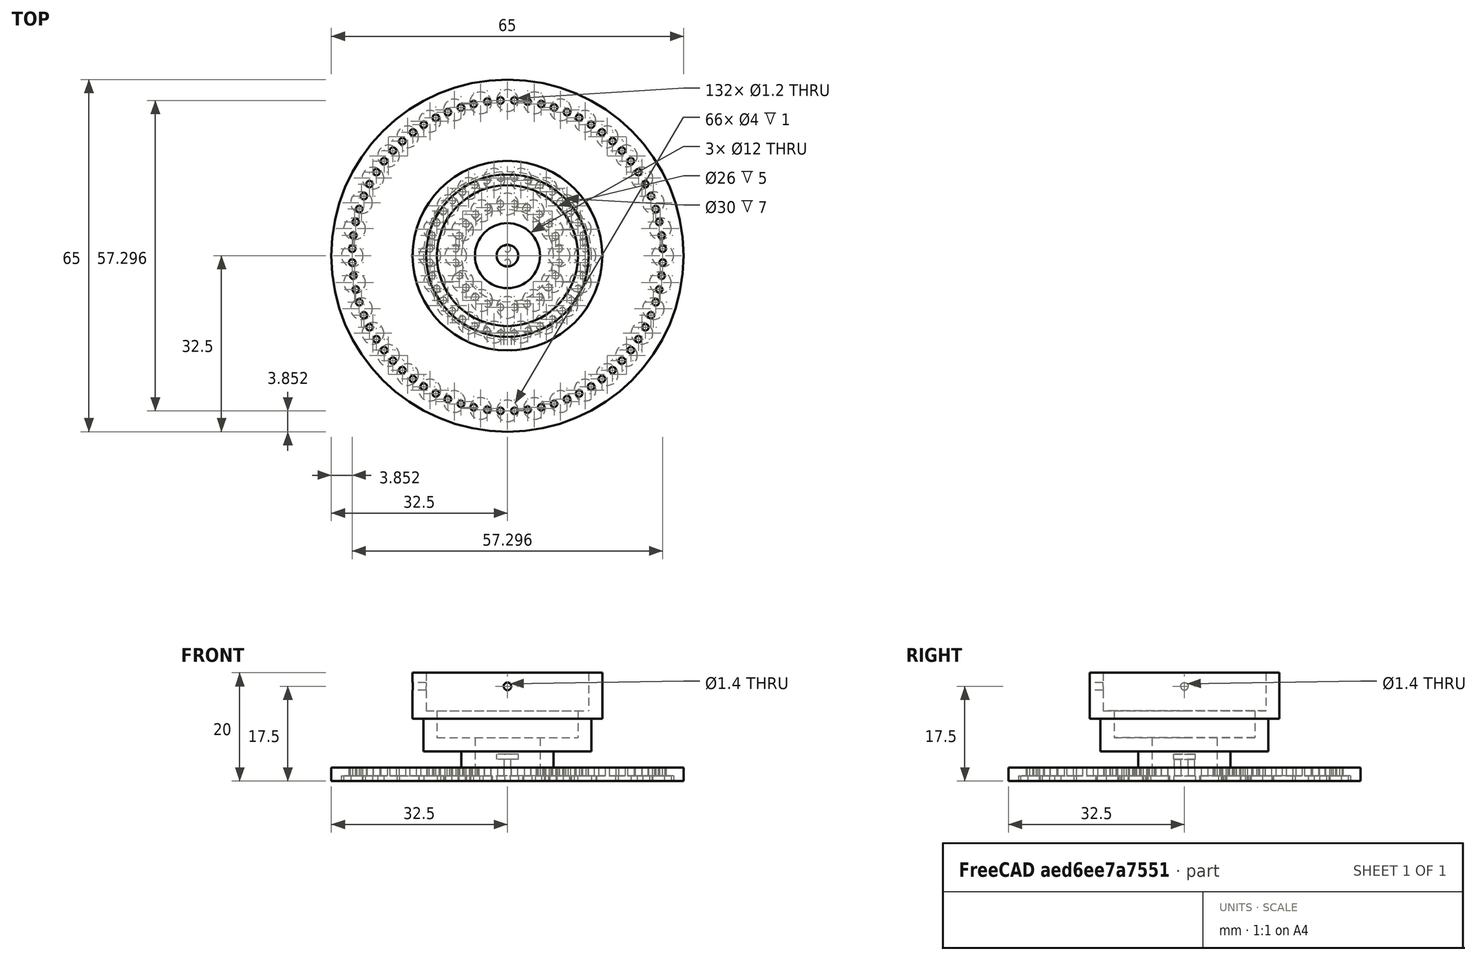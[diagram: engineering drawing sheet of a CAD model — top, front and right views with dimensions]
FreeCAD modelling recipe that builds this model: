
FCSTD DOCUMENT  (FreeCAD 0.16R6706 (Git))
Label: S2H-LED-ring-illuminator
License: All rights reserved
LicenseURL: http://en.wikipedia.org/wiki/All_rights_reserved
objects: Part::Cylinder×209, Part::MultiFuse×71, Part::Cut×7, Part::Thickness×3
note: 290 computed .brp shape members not serialized (recipe doc carries the construction recipe); baked Part::Feature solids carry a one-line shape summary decoded from their .brp

FEATURE [Part::Cylinder] Cylinder  label="grid base"
  Angle = 360
  Height = 2.5
  Radius = 32.5
FEATURE [Part::Cylinder] Cylinder001  label="cam slot"
  Angle = 360
  Height = 2.5
  Radius = 6
FEATURE [Part::Cut] Cut  label="grid plate"
  Base = -> Cylinder
  Tool = -> Cylinder001
FEATURE [Part::Cylinder] Cylinder002
  Angle = 360
  Height = 1
  Placement = pos=(0,0,1.5) rot=(0,0,1;0rad)
  Radius = 2
FEATURE [Part::Cylinder] Cylinder003
  Angle = 360
  Height = 2.5
  Placement = pos=(0,1.27,0) rot=(0,0,1;0rad)
  Radius = 0.6
FEATURE [Part::Cylinder] Cylinder004
  Angle = 360
  Height = 2.5
  Placement = pos=(0,-1.27,0) rot=(0,0,1;0rad)
  Radius = 0.6
FEATURE [Part::MultiFuse] Fusion  label="led slot template"
  Shapes = -> [Cylinder002,Cylinder003,Cylinder004]
FEATURE [Part::Cylinder] Cylinder005
  Angle = 360
  Height = 1
  Placement = pos=(0,0,1.5) rot=(0,0,1;0rad)
  Radius = 2
FEATURE [Part::Cylinder] Cylinder006
  Angle = 360
  Height = 2.5
  Placement = pos=(0,1.27,0) rot=(0,0,1;0rad)
  Radius = 0.6
FEATURE [Part::Cylinder] Cylinder007
  Angle = 360
  Height = 2.5
  Placement = pos=(0,-1.27,0) rot=(0,0,1;0rad)
  Radius = 0.6
FEATURE [Part::MultiFuse] Fusion001  label="led 1-01"
  Placement = pos=(9.5493,0,0) rot=(0,0,1;0rad)
  Shapes = -> [Cylinder005,Cylinder006,Cylinder007]
FEATURE [Part::Cylinder] Cylinder008
  Angle = 360
  Height = 1
  Placement = pos=(0,0,1.5) rot=(0,0,1;0rad)
  Radius = 2
FEATURE [Part::Cylinder] Cylinder009
  Angle = 360
  Height = 2.5
  Placement = pos=(0,1.27,0) rot=(0,0,1;0rad)
  Radius = 0.6
FEATURE [Part::Cylinder] Cylinder010
  Angle = 360
  Height = 2.5
  Placement = pos=(0,-1.27,0) rot=(0,0,1;0rad)
  Radius = 0.6
FEATURE [Part::MultiFuse] Fusion002  label="led 1-02"
  Placement = pos=(8.26993,4.77465,0) rot=(0,0,1;0.523599rad)
  Shapes = -> [Cylinder008,Cylinder009,Cylinder010]
FEATURE [Part::Cylinder] Cylinder011
  Angle = 360
  Height = 1
  Placement = pos=(0,0,1.5) rot=(0,0,1;0rad)
  Radius = 2
FEATURE [Part::Cylinder] Cylinder012
  Angle = 360
  Height = 2.5
  Placement = pos=(0,1.27,0) rot=(0,0,1;0rad)
  Radius = 0.6
FEATURE [Part::Cylinder] Cylinder013
  Angle = 360
  Height = 2.5
  Placement = pos=(0,-1.27,0) rot=(0,0,1;0rad)
  Radius = 0.6
FEATURE [Part::MultiFuse] Fusion003  label="led 1-03"
  Placement = pos=(4.77465,8.26993,0) rot=(0,0,1;1.0472rad)
  Shapes = -> [Cylinder011,Cylinder012,Cylinder013]
FEATURE [Part::Cylinder] Cylinder014
  Angle = 360
  Height = 1
  Placement = pos=(0,0,1.5) rot=(0,0,1;0rad)
  Radius = 2
FEATURE [Part::Cylinder] Cylinder015
  Angle = 360
  Height = 2.5
  Placement = pos=(0,1.27,0) rot=(0,0,1;0rad)
  Radius = 0.6
FEATURE [Part::Cylinder] Cylinder016
  Angle = 360
  Height = 2.5
  Placement = pos=(0,-1.27,0) rot=(0,0,1;0rad)
  Radius = 0.6
FEATURE [Part::MultiFuse] Fusion004  label="led 1-04"
  Placement = pos=(0,9.5493,0) rot=(0,0,1;1.5708rad)
  Shapes = -> [Cylinder014,Cylinder015,Cylinder016]
FEATURE [Part::Cylinder] Cylinder017
  Angle = 360
  Height = 1
  Placement = pos=(0,0,1.5) rot=(0,0,1;0rad)
  Radius = 2
FEATURE [Part::Cylinder] Cylinder018
  Angle = 360
  Height = 2.5
  Placement = pos=(0,1.27,0) rot=(0,0,1;0rad)
  Radius = 0.6
FEATURE [Part::Cylinder] Cylinder019
  Angle = 360
  Height = 2.5
  Placement = pos=(0,-1.27,0) rot=(0,0,1;0rad)
  Radius = 0.6
FEATURE [Part::MultiFuse] Fusion005  label="led 1-05"
  Placement = pos=(-4.77465,8.26993,0) rot=(0,0,1;2.0944rad)
  Shapes = -> [Cylinder017,Cylinder018,Cylinder019]
FEATURE [Part::Cylinder] Cylinder020
  Angle = 360
  Height = 1
  Placement = pos=(0,0,1.5) rot=(0,0,1;0rad)
  Radius = 2
FEATURE [Part::Cylinder] Cylinder021
  Angle = 360
  Height = 2.5
  Placement = pos=(0,1.27,0) rot=(0,0,1;0rad)
  Radius = 0.6
FEATURE [Part::Cylinder] Cylinder022
  Angle = 360
  Height = 2.5
  Placement = pos=(0,-1.27,0) rot=(0,0,1;0rad)
  Radius = 0.6
FEATURE [Part::MultiFuse] Fusion006  label="led 1-06"
  Placement = pos=(-8.26993,4.77465,0) rot=(0,0,1;2.61799rad)
  Shapes = -> [Cylinder020,Cylinder021,Cylinder022]
FEATURE [Part::Cylinder] Cylinder023
  Angle = 360
  Height = 1
  Placement = pos=(0,0,1.5) rot=(0,0,1;0rad)
  Radius = 2
FEATURE [Part::Cylinder] Cylinder024
  Angle = 360
  Height = 2.5
  Placement = pos=(0,1.27,0) rot=(0,0,1;0rad)
  Radius = 0.6
FEATURE [Part::Cylinder] Cylinder025
  Angle = 360
  Height = 2.5
  Placement = pos=(0,-1.27,0) rot=(0,0,1;0rad)
  Radius = 0.6
FEATURE [Part::MultiFuse] Fusion007  label="led 1-07"
  Placement = pos=(-9.5493,0,0) rot=(0,0,1;3.14159rad)
  Shapes = -> [Cylinder023,Cylinder024,Cylinder025]
FEATURE [Part::Cylinder] Cylinder026
  Angle = 360
  Height = 1
  Placement = pos=(0,0,1.5) rot=(0,0,1;0rad)
  Radius = 2
FEATURE [Part::Cylinder] Cylinder027
  Angle = 360
  Height = 2.5
  Placement = pos=(0,1.27,0) rot=(0,0,1;0rad)
  Radius = 0.6
FEATURE [Part::Cylinder] Cylinder028
  Angle = 360
  Height = 2.5
  Placement = pos=(0,-1.27,0) rot=(0,0,1;0rad)
  Radius = 0.6
FEATURE [Part::MultiFuse] Fusion008  label="led 1-08"
  Placement = pos=(-8.26993,-4.77465,0) rot=(0,0,1;3.66519rad)
  Shapes = -> [Cylinder026,Cylinder027,Cylinder028]
FEATURE [Part::Cylinder] Cylinder029
  Angle = 360
  Height = 1
  Placement = pos=(0,0,1.5) rot=(0,0,1;0rad)
  Radius = 2
FEATURE [Part::Cylinder] Cylinder030
  Angle = 360
  Height = 2.5
  Placement = pos=(0,1.27,0) rot=(0,0,1;0rad)
  Radius = 0.6
FEATURE [Part::Cylinder] Cylinder031
  Angle = 360
  Height = 2.5
  Placement = pos=(0,-1.27,0) rot=(0,0,1;0rad)
  Radius = 0.6
FEATURE [Part::MultiFuse] Fusion009  label="led 1-09"
  Placement = pos=(-4.77465,-8.26993,0) rot=(0,0,1;4.18879rad)
  Shapes = -> [Cylinder029,Cylinder030,Cylinder031]
FEATURE [Part::Cylinder] Cylinder032
  Angle = 360
  Height = 1
  Placement = pos=(0,0,1.5) rot=(0,0,1;0rad)
  Radius = 2
FEATURE [Part::Cylinder] Cylinder033
  Angle = 360
  Height = 2.5
  Placement = pos=(0,1.27,0) rot=(0,0,1;0rad)
  Radius = 0.6
FEATURE [Part::Cylinder] Cylinder034
  Angle = 360
  Height = 2.5
  Placement = pos=(0,-1.27,0) rot=(0,0,1;0rad)
  Radius = 0.6
FEATURE [Part::MultiFuse] Fusion010  label="led 1-10"
  Placement = pos=(0,-9.5493,0) rot=(0,0,-1;1.5708rad)
  Shapes = -> [Cylinder032,Cylinder033,Cylinder034]
FEATURE [Part::Cylinder] Cylinder035
  Angle = 360
  Height = 1
  Placement = pos=(0,0,1.5) rot=(0,0,1;0rad)
  Radius = 2
FEATURE [Part::Cylinder] Cylinder036
  Angle = 360
  Height = 2.5
  Placement = pos=(0,1.27,0) rot=(0,0,1;0rad)
  Radius = 0.6
FEATURE [Part::Cylinder] Cylinder037
  Angle = 360
  Height = 2.5
  Placement = pos=(0,-1.27,0) rot=(0,0,1;0rad)
  Radius = 0.6
FEATURE [Part::MultiFuse] Fusion011  label="led 1-11"
  Placement = pos=(4.77465,-8.26993,0) rot=(0,0,-1;1.0472rad)
  Shapes = -> [Cylinder035,Cylinder036,Cylinder037]
FEATURE [Part::Cylinder] Cylinder038
  Angle = 360
  Height = 1
  Placement = pos=(0,0,1.5) rot=(0,0,1;0rad)
  Radius = 2
FEATURE [Part::Cylinder] Cylinder039
  Angle = 360
  Height = 2.5
  Placement = pos=(0,1.27,0) rot=(0,0,1;0rad)
  Radius = 0.6
FEATURE [Part::Cylinder] Cylinder040
  Angle = 360
  Height = 2.5
  Placement = pos=(0,-1.27,0) rot=(0,0,1;0rad)
  Radius = 0.6
FEATURE [Part::MultiFuse] Fusion012  label="led 1-12"
  Placement = pos=(8.26993,-4.77465,0) rot=(0,0,-1;0.523599rad)
  Shapes = -> [Cylinder038,Cylinder039,Cylinder040]
FEATURE [Part::Cylinder] Cylinder041
  Angle = 360
  Height = 1
  Placement = pos=(0,0,1.5) rot=(0,0,1;0rad)
  Radius = 2
FEATURE [Part::Cylinder] Cylinder042
  Angle = 360
  Height = 2.5
  Placement = pos=(0,1.27,0) rot=(0,0,1;0rad)
  Radius = 0.6
FEATURE [Part::Cylinder] Cylinder043
  Angle = 360
  Height = 2.5
  Placement = pos=(0,-1.27,0) rot=(0,0,1;0rad)
  Radius = 0.6
FEATURE [Part::MultiFuse] Fusion013  label="led 2-01"
  Placement = pos=(14.3239,0,0) rot=(0,0,1;0rad)
  Shapes = -> [Cylinder041,Cylinder042,Cylinder043]
FEATURE [Part::Cylinder] Cylinder044
  Angle = 360
  Height = 1
  Placement = pos=(0,0,1.5) rot=(0,0,1;0rad)
  Radius = 2
FEATURE [Part::Cylinder] Cylinder045
  Angle = 360
  Height = 2.5
  Placement = pos=(0,1.27,0) rot=(0,0,1;0rad)
  Radius = 0.6
FEATURE [Part::Cylinder] Cylinder046
  Angle = 360
  Height = 2.5
  Placement = pos=(0,-1.27,0) rot=(0,0,1;0rad)
  Radius = 0.6
FEATURE [Part::MultiFuse] Fusion014  label="led 2-02"
  Placement = pos=(13.4601,4.89908,0) rot=(0,0,1;0.349066rad)
  Shapes = -> [Cylinder044,Cylinder045,Cylinder046]
FEATURE [Part::Cylinder] Cylinder047
  Angle = 360
  Height = 1
  Placement = pos=(0,0,1.5) rot=(0,0,1;0rad)
  Radius = 2
FEATURE [Part::Cylinder] Cylinder048
  Angle = 360
  Height = 2.5
  Placement = pos=(0,1.27,0) rot=(0,0,1;0rad)
  Radius = 0.6
FEATURE [Part::Cylinder] Cylinder049
  Angle = 360
  Height = 2.5
  Placement = pos=(0,-1.27,0) rot=(0,0,1;0rad)
  Radius = 0.6
FEATURE [Part::MultiFuse] Fusion015  label="led 2-03"
  Placement = pos=(10.9728,9.20725,0) rot=(0,0,1;0.698132rad)
  Shapes = -> [Cylinder047,Cylinder048,Cylinder049]
FEATURE [Part::Cylinder] Cylinder050
  Angle = 360
  Height = 1
  Placement = pos=(0,0,1.5) rot=(0,0,1;0rad)
  Radius = 2
FEATURE [Part::Cylinder] Cylinder051
  Angle = 360
  Height = 2.5
  Placement = pos=(0,1.27,0) rot=(0,0,1;0rad)
  Radius = 0.6
FEATURE [Part::Cylinder] Cylinder052
  Angle = 360
  Height = 2.5
  Placement = pos=(0,-1.27,0) rot=(0,0,1;0rad)
  Radius = 0.6
FEATURE [Part::MultiFuse] Fusion016  label="led 2-04"
  Placement = pos=(7.16197,12.4049,0) rot=(0,0,1;1.0472rad)
  Shapes = -> [Cylinder050,Cylinder051,Cylinder052]
FEATURE [Part::Cylinder] Cylinder053
  Angle = 360
  Height = 1
  Placement = pos=(0,0,1.5) rot=(0,0,1;0rad)
  Radius = 2
FEATURE [Part::Cylinder] Cylinder054
  Angle = 360
  Height = 2.5
  Placement = pos=(0,1.27,0) rot=(0,0,1;0rad)
  Radius = 0.6
FEATURE [Part::Cylinder] Cylinder055
  Angle = 360
  Height = 2.5
  Placement = pos=(0,-1.27,0) rot=(0,0,1;0rad)
  Radius = 0.6
FEATURE [Part::MultiFuse] Fusion017  label="led 2-05"
  Placement = pos=(2.48733,14.1063,0) rot=(0,0,1;1.39626rad)
  Shapes = -> [Cylinder053,Cylinder054,Cylinder055]
FEATURE [Part::Cylinder] Cylinder056
  Angle = 360
  Height = 1
  Placement = pos=(0,0,1.5) rot=(0,0,1;0rad)
  Radius = 2
FEATURE [Part::Cylinder] Cylinder057
  Angle = 360
  Height = 2.5
  Placement = pos=(0,1.27,0) rot=(0,0,1;0rad)
  Radius = 0.6
FEATURE [Part::Cylinder] Cylinder058
  Angle = 360
  Height = 2.5
  Placement = pos=(0,-1.27,0) rot=(0,0,1;0rad)
  Radius = 0.6
FEATURE [Part::MultiFuse] Fusion018  label="led 2-06"
  Placement = pos=(-2.48733,14.1063,0) rot=(0,0,1;1.74533rad)
  Shapes = -> [Cylinder056,Cylinder057,Cylinder058]
FEATURE [Part::Cylinder] Cylinder059
  Angle = 360
  Height = 1
  Placement = pos=(0,0,1.5) rot=(0,0,1;0rad)
  Radius = 2
FEATURE [Part::Cylinder] Cylinder060
  Angle = 360
  Height = 2.5
  Placement = pos=(0,1.27,0) rot=(0,0,1;0rad)
  Radius = 0.6
FEATURE [Part::Cylinder] Cylinder061
  Angle = 360
  Height = 2.5
  Placement = pos=(0,-1.27,0) rot=(0,0,1;0rad)
  Radius = 0.6
FEATURE [Part::MultiFuse] Fusion019  label="led 2-07"
  Placement = pos=(-7.16197,12.4049,0) rot=(0,0,1;2.0944rad)
  Shapes = -> [Cylinder059,Cylinder060,Cylinder061]
FEATURE [Part::Cylinder] Cylinder062
  Angle = 360
  Height = 1
  Placement = pos=(0,0,1.5) rot=(0,0,1;0rad)
  Radius = 2
FEATURE [Part::Cylinder] Cylinder063
  Angle = 360
  Height = 2.5
  Placement = pos=(0,1.27,0) rot=(0,0,1;0rad)
  Radius = 0.6
FEATURE [Part::Cylinder] Cylinder064
  Angle = 360
  Height = 2.5
  Placement = pos=(0,-1.27,0) rot=(0,0,1;0rad)
  Radius = 0.6
FEATURE [Part::MultiFuse] Fusion020  label="led 2-08"
  Placement = pos=(-10.9728,9.20725,0) rot=(0,0,1;2.44346rad)
  Shapes = -> [Cylinder062,Cylinder063,Cylinder064]
FEATURE [Part::Cylinder] Cylinder065
  Angle = 360
  Height = 1
  Placement = pos=(0,0,1.5) rot=(0,0,1;0rad)
  Radius = 2
FEATURE [Part::Cylinder] Cylinder066
  Angle = 360
  Height = 2.5
  Placement = pos=(0,1.27,0) rot=(0,0,1;0rad)
  Radius = 0.6
FEATURE [Part::Cylinder] Cylinder067
  Angle = 360
  Height = 2.5
  Placement = pos=(0,-1.27,0) rot=(0,0,1;0rad)
  Radius = 0.6
FEATURE [Part::MultiFuse] Fusion021  label="led 2-09"
  Placement = pos=(-13.4601,4.89908,0) rot=(0,0,1;2.79253rad)
  Shapes = -> [Cylinder065,Cylinder066,Cylinder067]
FEATURE [Part::Cylinder] Cylinder068
  Angle = 360
  Height = 1
  Placement = pos=(0,0,1.5) rot=(0,0,1;0rad)
  Radius = 2
FEATURE [Part::Cylinder] Cylinder069
  Angle = 360
  Height = 2.5
  Placement = pos=(0,1.27,0) rot=(0,0,1;0rad)
  Radius = 0.6
FEATURE [Part::Cylinder] Cylinder070
  Angle = 360
  Height = 2.5
  Placement = pos=(0,-1.27,0) rot=(0,0,1;0rad)
  Radius = 0.6
FEATURE [Part::MultiFuse] Fusion022  label="led 2-10"
  Placement = pos=(-14.3239,0,0) rot=(0,0,1;3.14159rad)
  Shapes = -> [Cylinder068,Cylinder069,Cylinder070]
FEATURE [Part::Cylinder] Cylinder071
  Angle = 360
  Height = 1
  Placement = pos=(0,0,1.5) rot=(0,0,1;0rad)
  Radius = 2
FEATURE [Part::Cylinder] Cylinder072
  Angle = 360
  Height = 2.5
  Placement = pos=(0,1.27,0) rot=(0,0,1;0rad)
  Radius = 0.6
FEATURE [Part::Cylinder] Cylinder073
  Angle = 360
  Height = 2.5
  Placement = pos=(0,-1.27,0) rot=(0,0,1;0rad)
  Radius = 0.6
FEATURE [Part::MultiFuse] Fusion023  label="led 2-11"
  Placement = pos=(-13.4601,-4.89908,0) rot=(0,0,1;3.49066rad)
  Shapes = -> [Cylinder071,Cylinder072,Cylinder073]
FEATURE [Part::Cylinder] Cylinder074
  Angle = 360
  Height = 1
  Placement = pos=(0,0,1.5) rot=(0,0,1;0rad)
  Radius = 2
FEATURE [Part::Cylinder] Cylinder075
  Angle = 360
  Height = 2.5
  Placement = pos=(0,1.27,0) rot=(0,0,1;0rad)
  Radius = 0.6
FEATURE [Part::Cylinder] Cylinder076
  Angle = 360
  Height = 2.5
  Placement = pos=(0,-1.27,0) rot=(0,0,1;0rad)
  Radius = 0.6
FEATURE [Part::MultiFuse] Fusion024  label="led 2-12"
  Placement = pos=(-10.9728,-9.20725,0) rot=(0,0,1;3.83972rad)
  Shapes = -> [Cylinder074,Cylinder075,Cylinder076]
FEATURE [Part::Cylinder] Cylinder077
  Angle = 360
  Height = 1
  Placement = pos=(0,0,1.5) rot=(0,0,1;0rad)
  Radius = 2
FEATURE [Part::Cylinder] Cylinder078
  Angle = 360
  Height = 2.5
  Placement = pos=(0,1.27,0) rot=(0,0,1;0rad)
  Radius = 0.6
FEATURE [Part::Cylinder] Cylinder079
  Angle = 360
  Height = 2.5
  Placement = pos=(0,-1.27,0) rot=(0,0,1;0rad)
  Radius = 0.6
FEATURE [Part::MultiFuse] Fusion025  label="led 2-13"
  Placement = pos=(-7.16197,-12.4049,0) rot=(0,0,1;4.18879rad)
  Shapes = -> [Cylinder077,Cylinder078,Cylinder079]
FEATURE [Part::Cylinder] Cylinder080
  Angle = 360
  Height = 1
  Placement = pos=(0,0,1.5) rot=(0,0,1;0rad)
  Radius = 2
FEATURE [Part::Cylinder] Cylinder081
  Angle = 360
  Height = 2.5
  Placement = pos=(0,1.27,0) rot=(0,0,1;0rad)
  Radius = 0.6
FEATURE [Part::Cylinder] Cylinder082
  Angle = 360
  Height = 2.5
  Placement = pos=(0,-1.27,0) rot=(0,0,1;0rad)
  Radius = 0.6
FEATURE [Part::MultiFuse] Fusion026  label="led 2-14"
  Placement = pos=(-2.48733,-14.1063,0) rot=(0,0,-1;1.74533rad)
  Shapes = -> [Cylinder080,Cylinder081,Cylinder082]
FEATURE [Part::Cylinder] Cylinder083
  Angle = 360
  Height = 1
  Placement = pos=(0,0,1.5) rot=(0,0,1;0rad)
  Radius = 2
FEATURE [Part::Cylinder] Cylinder084
  Angle = 360
  Height = 2.5
  Placement = pos=(0,1.27,0) rot=(0,0,1;0rad)
  Radius = 0.6
FEATURE [Part::Cylinder] Cylinder085
  Angle = 360
  Height = 2.5
  Placement = pos=(0,-1.27,0) rot=(0,0,1;0rad)
  Radius = 0.6
FEATURE [Part::MultiFuse] Fusion027  label="led 2-15"
  Placement = pos=(2.48733,-14.1063,0) rot=(0,0,-1;1.39626rad)
  Shapes = -> [Cylinder083,Cylinder084,Cylinder085]
FEATURE [Part::Cylinder] Cylinder086
  Angle = 360
  Height = 1
  Placement = pos=(0,0,1.5) rot=(0,0,1;0rad)
  Radius = 2
FEATURE [Part::Cylinder] Cylinder087
  Angle = 360
  Height = 2.5
  Placement = pos=(0,1.27,0) rot=(0,0,1;0rad)
  Radius = 0.6
FEATURE [Part::Cylinder] Cylinder088
  Angle = 360
  Height = 2.5
  Placement = pos=(0,-1.27,0) rot=(0,0,1;0rad)
  Radius = 0.6
FEATURE [Part::MultiFuse] Fusion028  label="led 2-16"
  Placement = pos=(7.16197,-12.4049,0) rot=(0,0,-1;1.0472rad)
  Shapes = -> [Cylinder086,Cylinder087,Cylinder088]
FEATURE [Part::Cylinder] Cylinder089
  Angle = 360
  Height = 1
  Placement = pos=(0,0,1.5) rot=(0,0,1;0rad)
  Radius = 2
FEATURE [Part::Cylinder] Cylinder090
  Angle = 360
  Height = 2.5
  Placement = pos=(0,1.27,0) rot=(0,0,1;0rad)
  Radius = 0.6
FEATURE [Part::Cylinder] Cylinder091
  Angle = 360
  Height = 2.5
  Placement = pos=(0,-1.27,0) rot=(0,0,1;0rad)
  Radius = 0.6
FEATURE [Part::MultiFuse] Fusion029  label="led 2-17"
  Placement = pos=(10.9728,-9.20725,0) rot=(0,0,-1;0.698132rad)
  Shapes = -> [Cylinder089,Cylinder090,Cylinder091]
FEATURE [Part::Cylinder] Cylinder092
  Angle = 360
  Height = 1
  Placement = pos=(0,0,1.5) rot=(0,0,1;0rad)
  Radius = 2
FEATURE [Part::Cylinder] Cylinder093
  Angle = 360
  Height = 2.5
  Placement = pos=(0,1.27,0) rot=(0,0,1;0rad)
  Radius = 0.6
FEATURE [Part::Cylinder] Cylinder094
  Angle = 360
  Height = 2.5
  Placement = pos=(0,-1.27,0) rot=(0,0,1;0rad)
  Radius = 0.6
FEATURE [Part::MultiFuse] Fusion030  label="led 2-18"
  Placement = pos=(13.4601,-4.89908,0) rot=(0,0,-1;0.349066rad)
  Shapes = -> [Cylinder092,Cylinder093,Cylinder094]
FEATURE [Part::Cylinder] Cylinder095
  Angle = 360
  Height = 1
  Placement = pos=(0,0,1.5) rot=(0,0,1;0rad)
  Radius = 2
FEATURE [Part::Cylinder] Cylinder096
  Angle = 360
  Height = 2.5
  Placement = pos=(0,1.27,0) rot=(0,0,1;0rad)
  Radius = 0.6
FEATURE [Part::Cylinder] Cylinder097
  Angle = 360
  Height = 2.5
  Placement = pos=(0,-1.27,0) rot=(0,0,1;0rad)
  Radius = 0.6
FEATURE [Part::MultiFuse] Fusion033  label="led 3-01"
  Placement = pos=(28.6479,0,0) rot=(0,0,1;0rad)
  Shapes = -> [Cylinder095,Cylinder096,Cylinder097]
FEATURE [Part::Cylinder] Cylinder098
  Angle = 360
  Height = 1
  Placement = pos=(0,0,1.5) rot=(0,0,1;0rad)
  Radius = 2
FEATURE [Part::Cylinder] Cylinder099
  Angle = 360
  Height = 2.5
  Placement = pos=(0,1.27,0) rot=(0,0,1;0rad)
  Radius = 0.6
FEATURE [Part::Cylinder] Cylinder100
  Angle = 360
  Height = 2.5
  Placement = pos=(0,-1.27,0) rot=(0,0,1;0rad)
  Radius = 0.6
FEATURE [Part::MultiFuse] Fusion034  label="led 3-02"
  Placement = pos=(28.2127,4.97465,0) rot=(0,0,1;0.174533rad)
  Shapes = -> [Cylinder098,Cylinder099,Cylinder100]
FEATURE [Part::Cylinder] Cylinder101
  Angle = 360
  Height = 1
  Placement = pos=(0,0,1.5) rot=(0,0,1;0rad)
  Radius = 2
FEATURE [Part::Cylinder] Cylinder102
  Angle = 360
  Height = 2.5
  Placement = pos=(0,1.27,0) rot=(0,0,1;0rad)
  Radius = 0.6
FEATURE [Part::Cylinder] Cylinder103
  Angle = 360
  Height = 2.5
  Placement = pos=(0,-1.27,0) rot=(0,0,1;0rad)
  Radius = 0.6
FEATURE [Part::MultiFuse] Fusion035  label="led 3-03"
  Placement = pos=(26.9202,9.79816,0) rot=(0,0,1;0.349066rad)
  Shapes = -> [Cylinder101,Cylinder102,Cylinder103]
FEATURE [Part::Cylinder] Cylinder104
  Angle = 360
  Height = 1
  Placement = pos=(0,0,1.5) rot=(0,0,1;0rad)
  Radius = 2
FEATURE [Part::Cylinder] Cylinder105
  Angle = 360
  Height = 2.5
  Placement = pos=(0,1.27,0) rot=(0,0,1;0rad)
  Radius = 0.6
FEATURE [Part::Cylinder] Cylinder106
  Angle = 360
  Height = 2.5
  Placement = pos=(0,-1.27,0) rot=(0,0,1;0rad)
  Radius = 0.6
FEATURE [Part::MultiFuse] Fusion036  label="led 3-04"
  Placement = pos=(24.8098,14.3239,0) rot=(0,0,1;0.523599rad)
  Shapes = -> [Cylinder104,Cylinder105,Cylinder106]
FEATURE [Part::Cylinder] Cylinder107
  Angle = 360
  Height = 1
  Placement = pos=(0,0,1.5) rot=(0,0,1;0rad)
  Radius = 2
FEATURE [Part::Cylinder] Cylinder108
  Angle = 360
  Height = 2.5
  Placement = pos=(0,1.27,0) rot=(0,0,1;0rad)
  Radius = 0.6
FEATURE [Part::Cylinder] Cylinder109
  Angle = 360
  Height = 2.5
  Placement = pos=(0,-1.27,0) rot=(0,0,1;0rad)
  Radius = 0.6
FEATURE [Part::MultiFuse] Fusion037  label="led 3-05"
  Placement = pos=(21.9456,18.4145,0) rot=(0,0,1;0.698132rad)
  Shapes = -> [Cylinder107,Cylinder108,Cylinder109]
FEATURE [Part::Cylinder] Cylinder110
  Angle = 360
  Height = 1
  Placement = pos=(0,0,1.5) rot=(0,0,1;0rad)
  Radius = 2
FEATURE [Part::Cylinder] Cylinder111
  Angle = 360
  Height = 2.5
  Placement = pos=(0,1.27,0) rot=(0,0,1;0rad)
  Radius = 0.6
FEATURE [Part::Cylinder] Cylinder112
  Angle = 360
  Height = 2.5
  Placement = pos=(0,-1.27,0) rot=(0,0,1;0rad)
  Radius = 0.6
FEATURE [Part::MultiFuse] Fusion038  label="led 3-06"
  Placement = pos=(18.4145,21.9456,0) rot=(0,0,1;0.872665rad)
  Shapes = -> [Cylinder110,Cylinder111,Cylinder112]
FEATURE [Part::Cylinder] Cylinder113
  Angle = 360
  Height = 1
  Placement = pos=(0,0,1.5) rot=(0,0,1;0rad)
  Radius = 2
FEATURE [Part::Cylinder] Cylinder114
  Angle = 360
  Height = 2.5
  Placement = pos=(0,1.27,0) rot=(0,0,1;0rad)
  Radius = 0.6
FEATURE [Part::Cylinder] Cylinder115
  Angle = 360
  Height = 2.5
  Placement = pos=(0,-1.27,0) rot=(0,0,1;0rad)
  Radius = 0.6
FEATURE [Part::MultiFuse] Fusion039  label="led 3-07"
  Placement = pos=(14.3239,24.8098,0) rot=(0,0,1;1.0472rad)
  Shapes = -> [Cylinder113,Cylinder114,Cylinder115]
FEATURE [Part::Cylinder] Cylinder116
  Angle = 360
  Height = 1
  Placement = pos=(0,0,1.5) rot=(0,0,1;0rad)
  Radius = 2
FEATURE [Part::Cylinder] Cylinder117
  Angle = 360
  Height = 2.5
  Placement = pos=(0,1.27,0) rot=(0,0,1;0rad)
  Radius = 0.6
FEATURE [Part::Cylinder] Cylinder118
  Angle = 360
  Height = 2.5
  Placement = pos=(0,-1.27,0) rot=(0,0,1;0rad)
  Radius = 0.6
FEATURE [Part::MultiFuse] Fusion040  label="led 3-08"
  Placement = pos=(9.79816,26.9202,0) rot=(0,0,1;1.22173rad)
  Shapes = -> [Cylinder116,Cylinder117,Cylinder118]
FEATURE [Part::Cylinder] Cylinder119
  Angle = 360
  Height = 1
  Placement = pos=(0,0,1.5) rot=(0,0,1;0rad)
  Radius = 2
FEATURE [Part::Cylinder] Cylinder120
  Angle = 360
  Height = 2.5
  Placement = pos=(0,1.27,0) rot=(0,0,1;0rad)
  Radius = 0.6
FEATURE [Part::Cylinder] Cylinder121
  Angle = 360
  Height = 2.5
  Placement = pos=(0,-1.27,0) rot=(0,0,1;0rad)
  Radius = 0.6
FEATURE [Part::MultiFuse] Fusion041  label="led 3-09"
  Placement = pos=(4.97465,28.2127,0) rot=(0,0,1;1.39626rad)
  Shapes = -> [Cylinder119,Cylinder120,Cylinder121]
FEATURE [Part::Cylinder] Cylinder122
  Angle = 360
  Height = 1
  Placement = pos=(0,0,1.5) rot=(0,0,1;0rad)
  Radius = 2
FEATURE [Part::Cylinder] Cylinder123
  Angle = 360
  Height = 2.5
  Placement = pos=(0,1.27,0) rot=(0,0,1;0rad)
  Radius = 0.6
FEATURE [Part::Cylinder] Cylinder124
  Angle = 360
  Height = 2.5
  Placement = pos=(0,-1.27,0) rot=(0,0,1;0rad)
  Radius = 0.6
FEATURE [Part::MultiFuse] Fusion042  label="led 3-10"
  Placement = pos=(0,28.6479,0) rot=(0,0,1;1.5708rad)
  Shapes = -> [Cylinder122,Cylinder123,Cylinder124]
FEATURE [Part::Cylinder] Cylinder125
  Angle = 360
  Height = 1
  Placement = pos=(0,0,1.5) rot=(0,0,1;0rad)
  Radius = 2
FEATURE [Part::Cylinder] Cylinder126
  Angle = 360
  Height = 2.5
  Placement = pos=(0,1.27,0) rot=(0,0,1;0rad)
  Radius = 0.6
FEATURE [Part::Cylinder] Cylinder127
  Angle = 360
  Height = 2.5
  Placement = pos=(0,-1.27,0) rot=(0,0,1;0rad)
  Radius = 0.6
FEATURE [Part::MultiFuse] Fusion043  label="led 3-11"
  Placement = pos=(-4.97465,28.2127,0) rot=(0,0,1;1.74533rad)
  Shapes = -> [Cylinder125,Cylinder126,Cylinder127]
FEATURE [Part::Cylinder] Cylinder128
  Angle = 360
  Height = 1
  Placement = pos=(0,0,1.5) rot=(0,0,1;0rad)
  Radius = 2
FEATURE [Part::Cylinder] Cylinder129
  Angle = 360
  Height = 2.5
  Placement = pos=(0,1.27,0) rot=(0,0,1;0rad)
  Radius = 0.6
FEATURE [Part::Cylinder] Cylinder130
  Angle = 360
  Height = 2.5
  Placement = pos=(0,-1.27,0) rot=(0,0,1;0rad)
  Radius = 0.6
FEATURE [Part::MultiFuse] Fusion044  label="led 3-12"
  Placement = pos=(-9.79816,26.9202,0) rot=(0,0,1;1.91986rad)
  Shapes = -> [Cylinder128,Cylinder129,Cylinder130]
FEATURE [Part::Cylinder] Cylinder131
  Angle = 360
  Height = 1
  Placement = pos=(0,0,1.5) rot=(0,0,1;0rad)
  Radius = 2
FEATURE [Part::Cylinder] Cylinder132
  Angle = 360
  Height = 2.5
  Placement = pos=(0,1.27,0) rot=(0,0,1;0rad)
  Radius = 0.6
FEATURE [Part::Cylinder] Cylinder133
  Angle = 360
  Height = 2.5
  Placement = pos=(0,-1.27,0) rot=(0,0,1;0rad)
  Radius = 0.6
FEATURE [Part::MultiFuse] Fusion045  label="led 3-13"
  Placement = pos=(-14.3239,24.8098,0) rot=(0,0,1;2.0944rad)
  Shapes = -> [Cylinder131,Cylinder132,Cylinder133]
FEATURE [Part::Cylinder] Cylinder134
  Angle = 360
  Height = 1
  Placement = pos=(0,0,1.5) rot=(0,0,1;0rad)
  Radius = 2
FEATURE [Part::Cylinder] Cylinder135
  Angle = 360
  Height = 2.5
  Placement = pos=(0,1.27,0) rot=(0,0,1;0rad)
  Radius = 0.6
FEATURE [Part::Cylinder] Cylinder136
  Angle = 360
  Height = 2.5
  Placement = pos=(0,-1.27,0) rot=(0,0,1;0rad)
  Radius = 0.6
FEATURE [Part::MultiFuse] Fusion046  label="led 3-14"
  Placement = pos=(-18.4145,21.9456,0) rot=(0,0,1;2.26893rad)
  Shapes = -> [Cylinder134,Cylinder135,Cylinder136]
FEATURE [Part::Cylinder] Cylinder137
  Angle = 360
  Height = 1
  Placement = pos=(0,0,1.5) rot=(0,0,1;0rad)
  Radius = 2
FEATURE [Part::Cylinder] Cylinder138
  Angle = 360
  Height = 2.5
  Placement = pos=(0,1.27,0) rot=(0,0,1;0rad)
  Radius = 0.6
FEATURE [Part::Cylinder] Cylinder139
  Angle = 360
  Height = 2.5
  Placement = pos=(0,-1.27,0) rot=(0,0,1;0rad)
  Radius = 0.6
FEATURE [Part::MultiFuse] Fusion047  label="led 3-15"
  Placement = pos=(-21.9456,18.4145,0) rot=(0,0,1;2.44346rad)
  Shapes = -> [Cylinder137,Cylinder138,Cylinder139]
FEATURE [Part::Cylinder] Cylinder140
  Angle = 360
  Height = 1
  Placement = pos=(0,0,1.5) rot=(0,0,1;0rad)
  Radius = 2
FEATURE [Part::Cylinder] Cylinder141
  Angle = 360
  Height = 2.5
  Placement = pos=(0,1.27,0) rot=(0,0,1;0rad)
  Radius = 0.6
FEATURE [Part::Cylinder] Cylinder142
  Angle = 360
  Height = 2.5
  Placement = pos=(0,-1.27,0) rot=(0,0,1;0rad)
  Radius = 0.6
FEATURE [Part::MultiFuse] Fusion048  label="led 3-16"
  Placement = pos=(-24.8098,14.3239,0) rot=(0,0,1;2.61799rad)
  Shapes = -> [Cylinder140,Cylinder141,Cylinder142]
FEATURE [Part::Cylinder] Cylinder143
  Angle = 360
  Height = 1
  Placement = pos=(0,0,1.5) rot=(0,0,1;0rad)
  Radius = 2
FEATURE [Part::Cylinder] Cylinder144
  Angle = 360
  Height = 2.5
  Placement = pos=(0,1.27,0) rot=(0,0,1;0rad)
  Radius = 0.6
FEATURE [Part::Cylinder] Cylinder145
  Angle = 360
  Height = 2.5
  Placement = pos=(0,-1.27,0) rot=(0,0,1;0rad)
  Radius = 0.6
FEATURE [Part::MultiFuse] Fusion049  label="led 3-17"
  Placement = pos=(-26.9202,9.79816,0) rot=(0,0,1;2.79253rad)
  Shapes = -> [Cylinder143,Cylinder144,Cylinder145]
FEATURE [Part::Cylinder] Cylinder146
  Angle = 360
  Height = 1
  Placement = pos=(0,0,1.5) rot=(0,0,1;0rad)
  Radius = 2
FEATURE [Part::Cylinder] Cylinder147
  Angle = 360
  Height = 2.5
  Placement = pos=(0,1.27,0) rot=(0,0,1;0rad)
  Radius = 0.6
FEATURE [Part::Cylinder] Cylinder148
  Angle = 360
  Height = 2.5
  Placement = pos=(0,-1.27,0) rot=(0,0,1;0rad)
  Radius = 0.6
FEATURE [Part::MultiFuse] Fusion050  label="led 3-18"
  Placement = pos=(-28.2127,4.97465,0) rot=(0,0,1;2.96706rad)
  Shapes = -> [Cylinder146,Cylinder147,Cylinder148]
FEATURE [Part::Cylinder] Cylinder149
  Angle = 360
  Height = 1
  Placement = pos=(0,0,1.5) rot=(0,0,1;0rad)
  Radius = 2
FEATURE [Part::Cylinder] Cylinder150
  Angle = 360
  Height = 2.5
  Placement = pos=(0,1.27,0) rot=(0,0,1;0rad)
  Radius = 0.6
FEATURE [Part::Cylinder] Cylinder151
  Angle = 360
  Height = 2.5
  Placement = pos=(0,-1.27,0) rot=(0,0,1;0rad)
  Radius = 0.6
FEATURE [Part::MultiFuse] Fusion051  label="led 3-19"
  Placement = pos=(-28.6479,0,0) rot=(0,0,1;3.14159rad)
  Shapes = -> [Cylinder149,Cylinder150,Cylinder151]
FEATURE [Part::Cylinder] Cylinder152
  Angle = 360
  Height = 1
  Placement = pos=(0,0,1.5) rot=(0,0,1;0rad)
  Radius = 2
FEATURE [Part::Cylinder] Cylinder153
  Angle = 360
  Height = 2.5
  Placement = pos=(0,1.27,0) rot=(0,0,1;0rad)
  Radius = 0.6
FEATURE [Part::Cylinder] Cylinder154
  Angle = 360
  Height = 2.5
  Placement = pos=(0,-1.27,0) rot=(0,0,1;0rad)
  Radius = 0.6
FEATURE [Part::MultiFuse] Fusion052  label="led 3-20"
  Placement = pos=(-28.2127,-4.97465,0) rot=(0,0,1;3.31613rad)
  Shapes = -> [Cylinder152,Cylinder153,Cylinder154]
FEATURE [Part::Cylinder] Cylinder155
  Angle = 360
  Height = 1
  Placement = pos=(0,0,1.5) rot=(0,0,1;0rad)
  Radius = 2
FEATURE [Part::Cylinder] Cylinder156
  Angle = 360
  Height = 2.5
  Placement = pos=(0,1.27,0) rot=(0,0,1;0rad)
  Radius = 0.6
FEATURE [Part::Cylinder] Cylinder157
  Angle = 360
  Height = 2.5
  Placement = pos=(0,-1.27,0) rot=(0,0,1;0rad)
  Radius = 0.6
FEATURE [Part::MultiFuse] Fusion053  label="led 3-21"
  Placement = pos=(-26.9202,-9.79816,0) rot=(0,0,1;3.49066rad)
  Shapes = -> [Cylinder155,Cylinder156,Cylinder157]
FEATURE [Part::Cylinder] Cylinder158
  Angle = 360
  Height = 1
  Placement = pos=(0,0,1.5) rot=(0,0,1;0rad)
  Radius = 2
FEATURE [Part::Cylinder] Cylinder159
  Angle = 360
  Height = 2.5
  Placement = pos=(0,1.27,0) rot=(0,0,1;0rad)
  Radius = 0.6
FEATURE [Part::Cylinder] Cylinder160
  Angle = 360
  Height = 2.5
  Placement = pos=(0,-1.27,0) rot=(0,0,1;0rad)
  Radius = 0.6
FEATURE [Part::MultiFuse] Fusion054  label="led 3-22"
  Placement = pos=(-24.8098,-14.3239,0) rot=(0,0,1;3.66519rad)
  Shapes = -> [Cylinder158,Cylinder159,Cylinder160]
FEATURE [Part::Cylinder] Cylinder161
  Angle = 360
  Height = 1
  Placement = pos=(0,0,1.5) rot=(0,0,1;0rad)
  Radius = 2
FEATURE [Part::Cylinder] Cylinder162
  Angle = 360
  Height = 2.5
  Placement = pos=(0,1.27,0) rot=(0,0,1;0rad)
  Radius = 0.6
FEATURE [Part::Cylinder] Cylinder163
  Angle = 360
  Height = 2.5
  Placement = pos=(0,-1.27,0) rot=(0,0,1;0rad)
  Radius = 0.6
FEATURE [Part::MultiFuse] Fusion055  label="led 3-23"
  Placement = pos=(-21.9456,-18.4145,0) rot=(0,0,1;3.83972rad)
  Shapes = -> [Cylinder161,Cylinder162,Cylinder163]
FEATURE [Part::Cylinder] Cylinder164
  Angle = 360
  Height = 1
  Placement = pos=(0,0,1.5) rot=(0,0,1;0rad)
  Radius = 2
FEATURE [Part::Cylinder] Cylinder165
  Angle = 360
  Height = 2.5
  Placement = pos=(0,1.27,0) rot=(0,0,1;0rad)
  Radius = 0.6
FEATURE [Part::Cylinder] Cylinder166
  Angle = 360
  Height = 2.5
  Placement = pos=(0,-1.27,0) rot=(0,0,1;0rad)
  Radius = 0.6
FEATURE [Part::MultiFuse] Fusion056  label="led 3-24"
  Placement = pos=(-18.4145,-21.9456,0) rot=(0,0,1;4.01426rad)
  Shapes = -> [Cylinder164,Cylinder165,Cylinder166]
FEATURE [Part::MultiFuse] Fusion057  label="ring 1"
  Shapes = -> [Fusion001,Fusion002,Fusion003,Fusion004,Fusion005,Fusion006,Fusion007,Fusion008,Fusion009,Fusion010,Fusion011,Fusion012]
FEATURE [Part::Cut] Cut001
  Base = -> Cut
  Tool = -> Fusion057
FEATURE [Part::MultiFuse] Fusion058  label="ring 2"
  Shapes = -> [Fusion013,Fusion014,Fusion015,Fusion016,Fusion017,Fusion018,Fusion019,Fusion020,Fusion021,Fusion022,Fusion023,Fusion024,Fusion025,Fusion026,Fusion027,Fusion028,Fusion029,Fusion030]
FEATURE [Part::Cut] Cut002
  Base = -> Cut001
  Tool = -> Fusion058
FEATURE [Part::Cylinder] Cylinder167
  Angle = 360
  Height = 1
  Placement = pos=(0,0,1.5) rot=(0,0,1;0rad)
  Radius = 2
FEATURE [Part::Cylinder] Cylinder168
  Angle = 360
  Height = 2.5
  Placement = pos=(0,1.27,0) rot=(0,0,1;0rad)
  Radius = 0.6
FEATURE [Part::Cylinder] Cylinder169
  Angle = 360
  Height = 2.5
  Placement = pos=(0,-1.27,0) rot=(0,0,1;0rad)
  Radius = 0.6
FEATURE [Part::MultiFuse] Fusion059  label="led 3-25"
  Placement = pos=(-14.3239,-24.8098,0) rot=(0,0,1;4.18879rad)
  Shapes = -> [Cylinder167,Cylinder168,Cylinder169]
FEATURE [Part::Cylinder] Cylinder170
  Angle = 360
  Height = 1
  Placement = pos=(0,0,1.5) rot=(0,0,1;0rad)
  Radius = 2
FEATURE [Part::Cylinder] Cylinder171
  Angle = 360
  Height = 2.5
  Placement = pos=(0,1.27,0) rot=(0,0,1;0rad)
  Radius = 0.6
FEATURE [Part::Cylinder] Cylinder172
  Angle = 360
  Height = 2.5
  Placement = pos=(0,-1.27,0) rot=(0,0,1;0rad)
  Radius = 0.6
FEATURE [Part::MultiFuse] Fusion060  label="led 3-26"
  Placement = pos=(-9.79816,-26.9202,0) rot=(0,0,-1;1.91986rad)
  Shapes = -> [Cylinder170,Cylinder171,Cylinder172]
FEATURE [Part::Cylinder] Cylinder173
  Angle = 360
  Height = 1
  Placement = pos=(0,0,1.5) rot=(0,0,1;0rad)
  Radius = 2
FEATURE [Part::Cylinder] Cylinder174
  Angle = 360
  Height = 2.5
  Placement = pos=(0,1.27,0) rot=(0,0,1;0rad)
  Radius = 0.6
FEATURE [Part::Cylinder] Cylinder175
  Angle = 360
  Height = 2.5
  Placement = pos=(0,-1.27,0) rot=(0,0,1;0rad)
  Radius = 0.6
FEATURE [Part::MultiFuse] Fusion061  label="led 3-27"
  Placement = pos=(-4.97465,-28.2127,0) rot=(0,0,-1;1.74533rad)
  Shapes = -> [Cylinder173,Cylinder174,Cylinder175]
FEATURE [Part::Cylinder] Cylinder176
  Angle = 360
  Height = 1
  Placement = pos=(0,0,1.5) rot=(0,0,1;0rad)
  Radius = 2
FEATURE [Part::Cylinder] Cylinder177
  Angle = 360
  Height = 2.5
  Placement = pos=(0,1.27,0) rot=(0,0,1;0rad)
  Radius = 0.6
FEATURE [Part::Cylinder] Cylinder178
  Angle = 360
  Height = 2.5
  Placement = pos=(0,-1.27,0) rot=(0,0,1;0rad)
  Radius = 0.6
FEATURE [Part::MultiFuse] Fusion062  label="led 3-28"
  Placement = pos=(0,-28.6479,0) rot=(0,0,-1;1.5708rad)
  Shapes = -> [Cylinder176,Cylinder177,Cylinder178]
FEATURE [Part::Cylinder] Cylinder179
  Angle = 360
  Height = 1
  Placement = pos=(0,0,1.5) rot=(0,0,1;0rad)
  Radius = 2
FEATURE [Part::Cylinder] Cylinder180
  Angle = 360
  Height = 2.5
  Placement = pos=(0,1.27,0) rot=(0,0,1;0rad)
  Radius = 0.6
FEATURE [Part::Cylinder] Cylinder181
  Angle = 360
  Height = 2.5
  Placement = pos=(0,-1.27,0) rot=(0,0,1;0rad)
  Radius = 0.6
FEATURE [Part::MultiFuse] Fusion063  label="led 3-29"
  Placement = pos=(4.97465,-28.2127,0) rot=(0,0,-1;1.39626rad)
  Shapes = -> [Cylinder179,Cylinder180,Cylinder181]
FEATURE [Part::Cylinder] Cylinder182
  Angle = 360
  Height = 1
  Placement = pos=(0,0,1.5) rot=(0,0,1;0rad)
  Radius = 2
FEATURE [Part::Cylinder] Cylinder183
  Angle = 360
  Height = 2.5
  Placement = pos=(0,1.27,0) rot=(0,0,1;0rad)
  Radius = 0.6
FEATURE [Part::Cylinder] Cylinder184
  Angle = 360
  Height = 2.5
  Placement = pos=(0,-1.27,0) rot=(0,0,1;0rad)
  Radius = 0.6
FEATURE [Part::MultiFuse] Fusion064  label="led 3-30"
  Placement = pos=(9.79816,-26.9202,0) rot=(0,0,-1;1.22173rad)
  Shapes = -> [Cylinder182,Cylinder183,Cylinder184]
FEATURE [Part::Cylinder] Cylinder185
  Angle = 360
  Height = 1
  Placement = pos=(0,0,1.5) rot=(0,0,1;0rad)
  Radius = 2
FEATURE [Part::Cylinder] Cylinder186
  Angle = 360
  Height = 2.5
  Placement = pos=(0,1.27,0) rot=(0,0,1;0rad)
  Radius = 0.6
FEATURE [Part::Cylinder] Cylinder187
  Angle = 360
  Height = 2.5
  Placement = pos=(0,-1.27,0) rot=(0,0,1;0rad)
  Radius = 0.6
FEATURE [Part::MultiFuse] Fusion065  label="led 3-31"
  Placement = pos=(14.3239,-24.8098,0) rot=(0,0,-1;1.0472rad)
  Shapes = -> [Cylinder185,Cylinder186,Cylinder187]
FEATURE [Part::Cylinder] Cylinder188
  Angle = 360
  Height = 1
  Placement = pos=(0,0,1.5) rot=(0,0,1;0rad)
  Radius = 2
FEATURE [Part::Cylinder] Cylinder189
  Angle = 360
  Height = 2.5
  Placement = pos=(0,1.27,0) rot=(0,0,1;0rad)
  Radius = 0.6
FEATURE [Part::Cylinder] Cylinder190
  Angle = 360
  Height = 2.5
  Placement = pos=(0,-1.27,0) rot=(0,0,1;0rad)
  Radius = 0.6
FEATURE [Part::MultiFuse] Fusion066  label="led 3-32"
  Placement = pos=(18.4145,-21.9456,0) rot=(0,0,-1;0.872665rad)
  Shapes = -> [Cylinder188,Cylinder189,Cylinder190]
FEATURE [Part::Cylinder] Cylinder191
  Angle = 360
  Height = 1
  Placement = pos=(0,0,1.5) rot=(0,0,1;0rad)
  Radius = 2
FEATURE [Part::Cylinder] Cylinder192
  Angle = 360
  Height = 2.5
  Placement = pos=(0,1.27,0) rot=(0,0,1;0rad)
  Radius = 0.6
FEATURE [Part::Cylinder] Cylinder193
  Angle = 360
  Height = 2.5
  Placement = pos=(0,-1.27,0) rot=(0,0,1;0rad)
  Radius = 0.6
FEATURE [Part::MultiFuse] Fusion067  label="led 3-33"
  Placement = pos=(21.9456,-18.4145,0) rot=(0,0,-1;0.698132rad)
  Shapes = -> [Cylinder191,Cylinder192,Cylinder193]
FEATURE [Part::Cylinder] Cylinder194
  Angle = 360
  Height = 1
  Placement = pos=(0,0,1.5) rot=(0,0,1;0rad)
  Radius = 2
FEATURE [Part::Cylinder] Cylinder195
  Angle = 360
  Height = 2.5
  Placement = pos=(0,1.27,0) rot=(0,0,1;0rad)
  Radius = 0.6
FEATURE [Part::Cylinder] Cylinder196
  Angle = 360
  Height = 2.5
  Placement = pos=(0,-1.27,0) rot=(0,0,1;0rad)
  Radius = 0.6
FEATURE [Part::MultiFuse] Fusion068  label="led 3-34"
  Placement = pos=(24.8098,-14.3239,0) rot=(0,0,-1;0.523599rad)
  Shapes = -> [Cylinder194,Cylinder195,Cylinder196]
FEATURE [Part::Cylinder] Cylinder197
  Angle = 360
  Height = 1
  Placement = pos=(0,0,1.5) rot=(0,0,1;0rad)
  Radius = 2
FEATURE [Part::Cylinder] Cylinder198
  Angle = 360
  Height = 2.5
  Placement = pos=(0,1.27,0) rot=(0,0,1;0rad)
  Radius = 0.6
FEATURE [Part::Cylinder] Cylinder199
  Angle = 360
  Height = 2.5
  Placement = pos=(0,-1.27,0) rot=(0,0,1;0rad)
  Radius = 0.6
FEATURE [Part::MultiFuse] Fusion069  label="led 3-35"
  Placement = pos=(26.9202,-9.79816,0) rot=(0,0,-1;0.349066rad)
  Shapes = -> [Cylinder197,Cylinder198,Cylinder199]
FEATURE [Part::Cylinder] Cylinder200
  Angle = 360
  Height = 1
  Placement = pos=(0,0,1.5) rot=(0,0,1;0rad)
  Radius = 2
FEATURE [Part::Cylinder] Cylinder201
  Angle = 360
  Height = 2.5
  Placement = pos=(0,1.27,0) rot=(0,0,1;0rad)
  Radius = 0.6
FEATURE [Part::Cylinder] Cylinder202
  Angle = 360
  Height = 2.5
  Placement = pos=(0,-1.27,0) rot=(0,0,1;0rad)
  Radius = 0.6
FEATURE [Part::MultiFuse] Fusion070  label="led 3-36"
  Placement = pos=(28.2127,-4.97465,0) rot=(0,0,-1;0.174533rad)
  Shapes = -> [Cylinder200,Cylinder201,Cylinder202]
FEATURE [Part::MultiFuse] Fusion071  label="ring 3"
  Shapes = -> [Fusion033,Fusion034,Fusion035,Fusion036,Fusion037,Fusion038,Fusion039,Fusion040,Fusion041,Fusion042,Fusion043,Fusion044,Fusion045,Fusion046,Fusion047,Fusion048,Fusion049,Fusion050,Fusion051,Fusion052,Fusion053,Fusion054,Fusion055,Fusion056,Fusion059,Fusion060,Fusion061,Fusion062,Fusion063,Fusion064,Fusion065,Fusion066,Fusion067,Fusion068,Fusion069,Fusion070]
FEATURE [Part::Cut] Cut003
  Base = -> Cut002
  Tool = -> Fusion071
FEATURE [Part::Cylinder] Cylinder203  label="Cylinder"
  Angle = 360
  Height = 3
  Placement = pos=(0,0,-3) rot=(0,0,1;0rad)
  Radius = 6
FEATURE [Part::Thickness] Thickness
  Faces = -> Cylinder203 [Face3,Face2]
  Intersection = false
  Join = 0
  Mode = 0
  SelfIntersection = false
  Value = 2.5
FEATURE [Part::Cylinder] Cylinder204  label="Cylinder203"
  Angle = 360
  Height = 5
  Placement = pos=(0,0,-10.5) rot=(0,0,1;0rad)
  Radius = 13
FEATURE [Part::Thickness] Thickness001
  Faces = -> Cylinder204 [Face3]
  Intersection = false
  Join = 2
  Mode = 0
  SelfIntersection = false
  Value = 2.5
FEATURE [Part::Cylinder] Cylinder205  label="Cylinder204"
  Angle = 360
  Height = 10
  Placement = pos=(0,0,-10) rot=(0,0,1;0rad)
  Radius = 6
FEATURE [Part::Cut] Cut004
  Base = -> Thickness001
  Tool = -> Cylinder205
FEATURE [Part::Cylinder] Cylinder206  label="Cylinder205"
  Angle = 360
  Height = 8.5
  Radius = 15
FEATURE [Part::Thickness] Thickness002
  Faces = -> Cylinder206 [Face3,Face2]
  Intersection = false
  Join = 0
  Mode = 0
  Placement = pos=(0,0,-17.5) rot=(0,0,1;0rad)
  SelfIntersection = false
  Value = 2.5
FEATURE [Part::Cylinder] Cylinder207  label="Cylinder206"
  Angle = 360
  Height = 10
  Placement = pos=(0,-10,-15) rot=(1,0,0;1.5708rad)
  Radius = 0.7
FEATURE [Part::Cylinder] Cylinder208  label="Cylinder207"
  Angle = 360
  Height = 10
  Placement = pos=(10,0,-15) rot=(0,1,0;1.5708rad)
  Radius = 0.7
FEATURE [Part::Cut] Cut005
  Base = -> Thickness002
  Tool = -> Cylinder207
FEATURE [Part::Cut] Cut006
  Base = -> Cut005
  Tool = -> Cylinder208
FEATURE [Part::MultiFuse] Fusion072
  Placement = pos=(0,0,0) rot=(0,1,0;3.14159rad)
  Shapes = -> [Cut003,Thickness,Cut004,Cut006]
